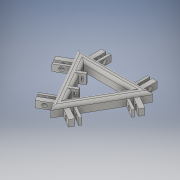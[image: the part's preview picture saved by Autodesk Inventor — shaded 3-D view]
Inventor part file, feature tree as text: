
AUTODESK INVENTOR PART (.ipt)
format: ipt  version: 2016 (Build 200138000, 138)  size: 305,664 bytes
history: native  units: in
note: dims shown in document units (in); Inventor stores cm internally (conversion verified against a paired STEP export)
features: extrude x9, sketch x9, fillet x1
ambient origin geometry x8: Origin, YZ Plane, XZ Plane, XY Plane, X Axis, Y Axis, Z Axis, Center Point
bodies: Solid1 (feature_tree)
feature tree (19):
  extrude  "Extrusion1"  Depth=1.9685in
  extrude  "Extrusion3"  Depth=0.3937in
  extrude  "Extrusion4"  Depth=0.2756in
  extrude  "Extrusion5"  Depth=0.0984in
  extrude  "Extrusion6"  Depth=0.1969in
  extrude  "Extrusion7"  Depth=0.1181in
  extrude  "Extrusion8"  Depth=0.2756in
  extrude  "Extrusion9"  Depth=0.2953in
  extrude  "Extrusion10"  Depth=2.3622in TaperAngle=0.0deg
  fillet  "Fillet1"  Radius=0.3937in
  sketch  "Sketch1"  dims[d18=3.1496in d19=1.9685in]
  sketch  "Sketch5"  dims[d20=0.3937in d21=0.0in d44=0.3937in]
  sketch  "Sketch6"  dims[d45=0.1969in d46=0.2756in]
  sketch  "Sketch7"  dims[d47=0.1181in d48=0.0984in]
  sketch  "Sketch8"  dims[d49=0.3937in d50=0.1969in]
  sketch  "Sketch9"  dims[d51=0.2756in d52=0.1181in]
  sketch  "Sketch10"  dims[d53=0.0984in d54=0.2756in]
  sketch  "Sketch11"  dims[d55=0.5906in d56=0.0in d57=0.2953in]
  sketch  "Sketch12"  dims[d58=0.1772in d59=2.3622in d60=0.0in d61=0.3937in d62=0.3937in d63=0.1969in d64=0.2756in d65=0.1181in d66=0.0984in d67=0.2756in d68=0.1969in d69=0.2756in d70=0.1181in d71=0.0984in d72=0.5906in d73=0.0in d74=0.2953in d75=90.0deg d76=0.1772in d77=2.3622in d78=0.0in d79=0.3937in d80=0.3937in d81=0.1969in d82=0.2756in d83=0.1181in d84=0.0984in d85=0.1969in d86=0.2756in d87=0.1181in d88=0.0984in d89=0.2756in d90=0.5906in d91=0.0in d92=0.2953in d93=0.1772in d94=2.3622in d95=0.0in d97=0.3543in d98=0.0in d99=0.3543in d100=180.0deg d101=0.1181in d102=0.1181in d103=0.2362in d104=0.0in d105=0.1181in d106=0.0787in d107=0.0787in d108=0.1575in d109=0.9843in d110=0.0in d111=0.1181in]
